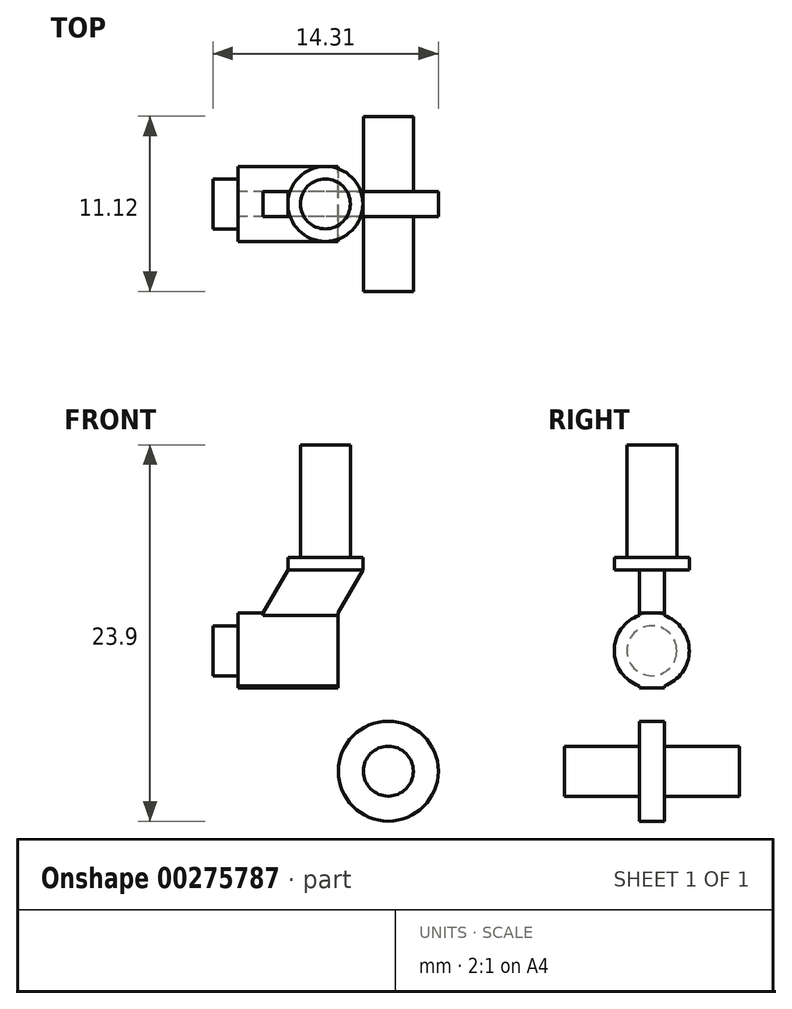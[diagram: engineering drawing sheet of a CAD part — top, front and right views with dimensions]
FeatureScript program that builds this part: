
annotation { "Feature Type Name" : "Feature", "Feature Type Description" : "" }
export const myFeature = defineFeature(function(context is Context, id is Id, definition is map)
    precondition{}
    {
        {
            var Q0;
            Q0=qCreatedBy(makeId("Top.planeOp"),FACE);
            var sketch = newSketch(context, id + "F0", { "sketchPlane" : qUnion([Q0])});
            skCircle(sketch, "E0", {"center": v(0, 0) * mm, "radius": 2.38 * mm});
            skCircle(sketch, "E1", {"center": v(0, 0) * mm, "radius": 1.59 * mm});
            skSolve(sketch);
        }
        {
            var Q0;
            Q0=makeQuery(id+"F0.imprint","IMPRINT",FACE,{"disambiguationData":[TD([[makeQuery(id+"F0.imprint","IMPRINT",EDGE,{"derivedFrom":sQuery(id+"F0.wireOp",EDGE,"E0")}),1.0]])]});
            extrude(context, id + "F1", {"entities" : qUnion([Q0]), "depth" : 0.8 * mm});
        }
        {
            var Q0;
            Q0=makeQuery(id+"F0.imprint","IMPRINT",FACE,{"disambiguationData":[TD([[makeQuery(id+"F0.imprint","IMPRINT",EDGE,{"derivedFrom":sQuery(id+"F0.wireOp",EDGE,"E1")}),1.0]])]});
            extrude(context, id + "F2", {"entities" : qUnion([Q0]), "operationType" : NewBodyOperationType.ADD, "depth" : 7.94 * mm});
        }
        {
            var Q0;
            Q0=qCreatedBy(makeId("Front.planeOp"),FACE);
            var sketch = newSketch(context, id + "F3", { "sketchPlane" : qUnion([Q0])});
            skLineSegment(sketch, "E2", {"start": v(0, 0) * mm, "end": v(-2.38, 0) * mm});
            skLineSegment(sketch, "E3", {"start": v(0, 0) * mm, "end": v(2.38, 0) * mm});
            skLineSegment(sketch, "E4", {"start": v(2.38, 0) * mm, "end": v(0.8, -2.75) * mm});
            skLineSegment(sketch, "E5", {"start": v(-2.38, 0) * mm, "end": v(-3.97, -2.75) * mm});
            skLineSegment(sketch, "E6", {"start": v(-3.97, -2.75) * mm, "end": v(0.8, -2.75) * mm});
            skLineSegment(sketch, "E7.bottom", {"start": v(0.8, -2.75) * mm, "end": v(-5.56, -2.75) * mm});
            skLineSegment(sketch, "E7.top", {"start": v(0.8, -7.51) * mm, "end": v(-5.56, -7.51) * mm});
            skLineSegment(sketch, "E7.left", {"start": v(0.8, -2.75) * mm, "end": v(0.8, -7.51) * mm});
            skLineSegment(sketch, "E8", {"start": v(-5.56, -5.13) * mm, "end": v(0.8, -5.13) * mm});
            skPoint(sketch, "E9", {"position": v(0.8, -3.54) * mm});
            skPoint(sketch, "E10.MirrorP", {"position": v(0.8, -6.72) * mm});
            skLineSegment(sketch, "E11.bottom", {"start": v(0.8, -6.72) * mm, "end": v(-7.14, -6.72) * mm});
            skLineSegment(sketch, "E11.left", {"start": v(0.8, -6.72) * mm, "end": v(0.8, -3.54) * mm});
            skLineSegment(sketch, "E11.right", {"start": v(-7.14, -6.72) * mm, "end": v(-7.14, -3.54) * mm});
            skLineSegment(sketch, "E12", {"start": v(-7.14, -5.13) * mm, "end": v(-5.56, -5.13) * mm});
            skLineSegment(sketch, "E13", {"start": v(-5.56, -2.75) * mm, "end": v(-5.56, -3.54) * mm});
            skLineSegment(sketch, "E14", {"start": v(-7.14, -3.54) * mm, "end": v(-5.56, -3.54) * mm});
            skLineSegment(sketch, "E15.MirrorCS", {"start": v(-7.14, -6.72) * mm, "end": v(-5.56, -6.72) * mm});
            skLineSegment(sketch, "E16.MirrorCS", {"start": v(-5.56, -7.51) * mm, "end": v(-5.56, -6.72) * mm});
            skLineSegment(sketch, "E17", {"start": v(0.8, -7.51) * mm, "end": v(3.04, -9.76) * mm});
            skLineSegment(sketch, "E18", {"start": v(-5.56, -7.51) * mm, "end": v(1.18, -14.25) * mm});
            skLineSegment(sketch, "E19", {"start": v(1.18, -14.25) * mm, "end": v(3.04, -9.76) * mm});
            skLineSegment(sketch, "E20.top", {"start": v(-3.97, -3.54) * mm, "end": v(0.8, -3.54) * mm});
            skLineSegment(sketch, "E20.left", {"start": v(-3.97, -2.75) * mm, "end": v(-3.97, -3.54) * mm});
            skLineSegment(sketch, "E20.right", {"start": v(0.8, -2.75) * mm, "end": v(0.8, -3.54) * mm});
            skCircle(sketch, "E21", {"center": v(4, -12.78) * mm, "radius": 3.18 * mm});
            skPoint(sketch, "E21.first.point", {"position": v(1.18, -14.25) * mm});
            skPoint(sketch, "E21.third.point", {"position": v(7.15, -13.17) * mm});
            skLineSegment(sketch, "E22", {"start": v(4, -12.78) * mm, "end": v(7.17, -12.78) * mm});
            skSolve(sketch);
        }
        {
            var Q0;
            Q0=makeQuery(id+"F3.imprint","IMPRINT",FACE,{"disambiguationData":[TD([[makeQuery(id+"F3.imprint","IMPRINT",EDGE,{"derivedFrom":sQuery(id+"F3.wireOp",EDGE,"E2")}),1.0]])]});
            var Q1;
            Q1=makeQuery(id+"F3.imprint","IMPRINT",FACE,{"disambiguationData":[TD([[makeQuery(id+"F3.imprint","IMPRINT",EDGE,{"derivedFrom":sQuery(id+"F3.wireOp",EDGE,"E6")}),-1.0]])]});
            var Q2;
            Q2=makeQuery(id+"F3.imprint","IMPRINT",FACE,{"disambiguationData":[TD([[makeQuery(id+"F3.imprint","IMPRINT",EDGE,{"derivedFrom":sQuery(id+"F3.wireOp",EDGE,"E7.left")}),-1.0]])]});
            var Q3;
            Q3=makeQuery(id+"F3.imprint","IMPRINT",FACE,{"disambiguationData":[TD([[makeQuery(id+"F3.imprint","IMPRINT",EDGE,{"derivedFrom":sQuery(id+"F3.wireOp",EDGE,"E7.top")}),1.0]])]});
            var Q4;
            {var subQ0=sQuery(id+"F3.wireOp",EDGE,"E19");Q4=makeQuery(id+"F3.imprint","IMPRINT",FACE,{"disambiguationData":[TD([[makeQuery(id+"F3.imprint","IMPRINT",EDGE,{"derivedFrom":subQ0}),1.0]])]});}
            var Q5;
            {var subQ0=sQuery(id+"F3.wireOp",EDGE,"E19");Q5=makeQuery(id+"F3.imprint","IMPRINT",FACE,{"disambiguationData":[TD([[makeQuery(id+"F3.imprint","IMPRINT",EDGE,{"derivedFrom":subQ0}),-1.0]])]});}
            extrude(context, id + "F4", {"entities" : qUnion([Q0, Q1, Q2, Q3, Q4, Q5]), "operationType" : NewBodyOperationType.ADD, "endBound" : BoundingType.SYMMETRIC, "depth" : 1.59 * mm});
        }
        {
            var Q0;
            Q0=makeQuery(id+"F3.imprint","IMPRINT",FACE,{"disambiguationData":[TD([[makeQuery(id+"F3.imprint","IMPRINT",EDGE,{"derivedFrom":sQuery(id+"F3.wireOp",EDGE,"E7.bottom")}),1.0]])]});
            var Q1;
            Q1=makeQuery(id+"F3.imprint","IMPRINT",FACE,{"disambiguationData":[TD([[makeQuery(id+"F3.imprint","IMPRINT",EDGE,{"derivedFrom":sQuery(id+"F3.wireOp",EDGE,"E6")}),-1.0]])]});
            var Q2;
            Q2=sQuery(id+"F3.wireOp",EDGE,"E8");
            revolve(context, id + "F5", {"operationType" : NewBodyOperationType.ADD, "entities" : qUnion([Q0, Q1]), "axis" : qUnion([Q2]), "revolveType" : RevolveType.FULL});
        }
        {
            var Q0;
            Q0=makeQuery(id+"F4.opExtrude","CAP_FACE",FACE,{"disambiguationData":[OSD([sQuery(id+"F3.wireOp",EDGE,"E7.left"),sQuery(id+"F3.wireOp",EDGE,"E11.bottom"),sQuery(id+"F3.wireOp",EDGE,"E16.MirrorCS"),sQuery(id+"F3.wireOp",EDGE,"E17"),sQuery(id+"F3.wireOp",EDGE,"E18"),sQuery(id+"F3.wireOp",EDGE,"E21")])],"isStart":false});
            var sketch = newSketch(context, id + "F6", { "sketchPlane" : qUnion([Q0])});
            skCircle(sketch, "E23", {"center": v(4, -12.78) * mm, "radius": 1.59 * mm});
            skSolve(sketch);
        }
        {
            var Q0;
            Q0=qSketchRegion(id+"F6",true);
            extrude(context, id + "F7", {"entities" : qUnion([Q0]), "operationType" : NewBodyOperationType.ADD, "depth" : 4.76 * mm});
        }
        {
            var Q0;
            Q0=makeQuery(id+"F4.opExtrude","CAP_FACE",FACE,{"disambiguationData":[OSD([sQuery(id+"F3.wireOp",EDGE,"E7.left"),sQuery(id+"F3.wireOp",EDGE,"E11.bottom"),sQuery(id+"F3.wireOp",EDGE,"E16.MirrorCS"),sQuery(id+"F3.wireOp",EDGE,"E17"),sQuery(id+"F3.wireOp",EDGE,"E18"),sQuery(id+"F3.wireOp",EDGE,"E21")])],"isStart":true});
            var sketch = newSketch(context, id + "F8", { "sketchPlane" : qUnion([Q0])});
            skCircle(sketch, "E24", {"center": v(-4, -12.78) * mm, "radius": 1.59 * mm});
            skSolve(sketch);
        }
        {
            var Q0;
            Q0=qSketchRegion(id+"F8",true);
            extrude(context, id + "F9", {"entities" : qUnion([Q0]), "operationType" : NewBodyOperationType.ADD, "depth" : 4.76 * mm});
        }
    });
